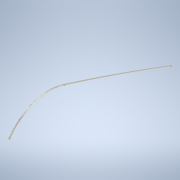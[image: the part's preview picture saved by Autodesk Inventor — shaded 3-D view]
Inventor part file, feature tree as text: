
AUTODESK INVENTOR PART (.ipt)
format: ipt  version: 2022 (Build 260153000, 153)  size: 123,392 bytes
history: native  units: in
note: dims shown in document units (in); Inventor stores cm internally (conversion verified against a paired STEP export)
features: sketch x2, sweep x1
ambient origin geometry x8: Origin, YZ Plane, XZ Plane, XY Plane, X Axis, Y Axis, Z Axis, Center Point
bodies: Solid1 (feature_tree)
feature tree (3):
  sweep  "Sweep1"
  sketch  "Sketch3"  dims[d10=0.001in d11=0.0059in]
  sketch  "Sketch4"  dims[d12=0.013in d13=0.1122in d14=90.0deg d15=0.0in d16=0.0in]
